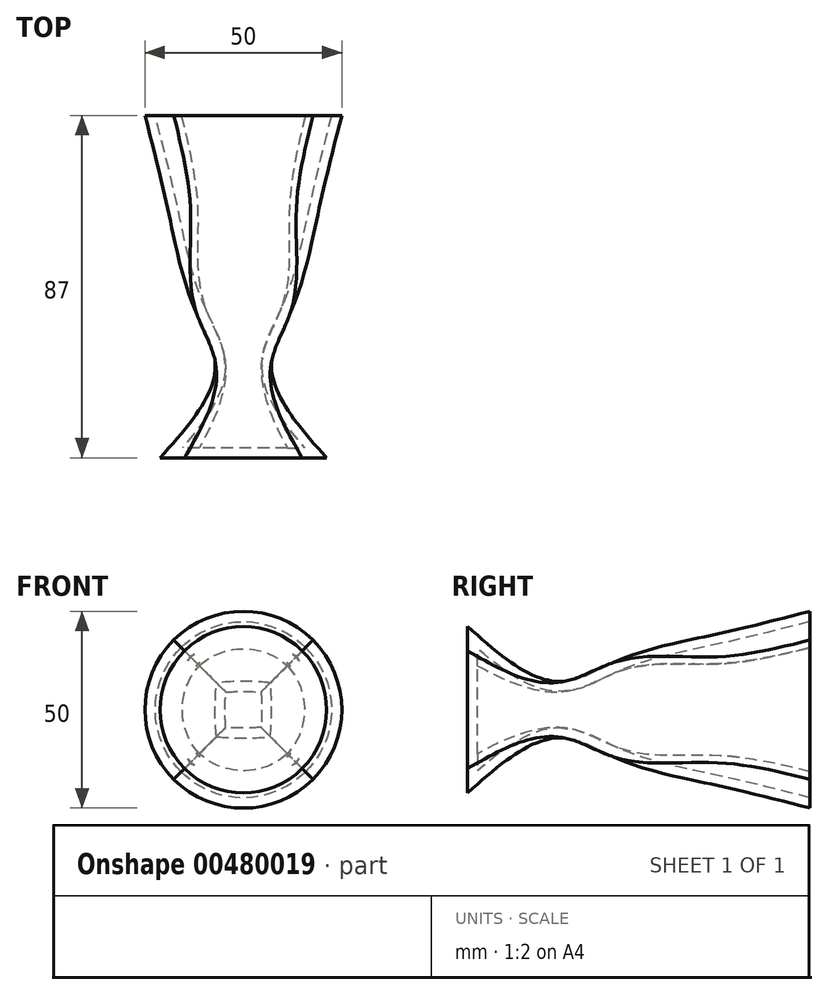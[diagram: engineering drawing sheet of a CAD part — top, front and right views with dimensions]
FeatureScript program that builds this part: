
annotation { "Feature Type Name" : "Feature", "Feature Type Description" : "" }
export const myFeature = defineFeature(function(context is Context, id is Id, definition is map)
    precondition{}
    {
        {
            var Q0;
            Q0=qCreatedBy(makeId("Front.planeOp"),FACE);
            var sketch = newSketch(context, id + "F0", { "sketchPlane" : qUnion([Q0])});
            skCircle(sketch, "E0", {"center": v(0, 0) * mm, "radius": 25 * mm});
            skSolve(sketch);
        }
        {
            var Q0;
            Q0=qCreatedBy(makeId("Front.planeOp"),FACE);
            cPlane(context, id + "F1", {"entities" : qUnion([Q0]), "cplaneType" : CPlaneType.OFFSET, "offset" : 25 * mm, "width" : 152.4 * mm, "height" : 152.4 * mm});
        }
        {
            var Q0;
            Q0=qCreatedBy(id+"F1.planeOp",FACE);
            var sketch = newSketch(context, id + "F2", { "sketchPlane" : qUnion([Q0])});
            skCircle(sketch, "E1", {"center": v(0, 0) * mm, "radius": 18.94 * mm});
            skSolve(sketch);
        }
        {
            var Q0;
            Q0=qCreatedBy(id+"F1.planeOp",FACE);
            cPlane(context, id + "F3", {"entities" : qUnion([Q0]), "cplaneType" : CPlaneType.OFFSET, "offset" : 25 * mm, "width" : 152.4 * mm, "height" : 152.4 * mm});
        }
        {
            var Q0;
            Q0=qCreatedBy(id+"F3.planeOp",FACE);
            var sketch = newSketch(context, id + "F4", { "sketchPlane" : qUnion([Q0])});
            skLineSegment(sketch, "E2.bottom", {"start": v(-11.96, 11.96) * mm, "end": v(11.96, 11.96) * mm});
            skLineSegment(sketch, "E2.top", {"start": v(-11.96, -11.96) * mm, "end": v(11.96, -11.96) * mm});
            skLineSegment(sketch, "E2.left", {"start": v(-11.96, 11.96) * mm, "end": v(-11.96, -11.96) * mm});
            skLineSegment(sketch, "E2.right", {"start": v(11.96, 11.96) * mm, "end": v(11.96, -11.96) * mm});
            skPoint(sketch, "E2.middle", {"position": v(0, 0) * mm});
            skSolve(sketch);
        }
        {
            var Q0;
            Q0=qCreatedBy(id+"F3.planeOp",FACE);
            cPlane(context, id + "F5", {"entities" : qUnion([Q0]), "cplaneType" : CPlaneType.OFFSET, "offset" : 12 * mm, "width" : 152.4 * mm, "height" : 152.4 * mm});
        }
        {
            var Q0;
            Q0=qCreatedBy(id+"F5.planeOp",FACE);
            var sketch = newSketch(context, id + "F6", { "sketchPlane" : qUnion([Q0])});
            skLineSegment(sketch, "E3.bottom", {"start": v(-7.25, 7.25) * mm, "end": v(7.25, 7.25) * mm});
            skLineSegment(sketch, "E3.top", {"start": v(-7.25, -7.25) * mm, "end": v(7.25, -7.25) * mm});
            skLineSegment(sketch, "E3.left", {"start": v(-7.25, 7.25) * mm, "end": v(-7.25, -7.25) * mm});
            skLineSegment(sketch, "E3.right", {"start": v(7.25, 7.25) * mm, "end": v(7.25, -7.25) * mm});
            skPoint(sketch, "E3.middle", {"position": v(0, 0) * mm});
            skSolve(sketch);
        }
        {
            var Q0;
            Q0=qCreatedBy(id+"F5.planeOp",FACE);
            cPlane(context, id + "F7", {"entities" : qUnion([Q0]), "cplaneType" : CPlaneType.OFFSET, "offset" : 25 * mm, "width" : 152.4 * mm, "height" : 152.4 * mm});
        }
        {
            var Q0;
            Q0=qCreatedBy(id+"F7.planeOp",FACE);
            var sketch = newSketch(context, id + "F8", { "sketchPlane" : qUnion([Q0])});
            skCircle(sketch, "E4", {"center": v(0, 0) * mm, "radius": 21.14 * mm});
            skSolve(sketch);
        }
        {
            var Q0;
            Q0=makeQuery(id+"F8.imprint","IMPRINT",FACE,{"disambiguationData":[TD([[makeQuery(id+"F8.imprint","IMPRINT",EDGE,{"derivedFrom":sQuery(id+"F8.wireOp",EDGE,"E4")}),1.0]])]});
            var Q1;
            Q1=makeQuery(id+"F6.imprint","IMPRINT",FACE,{"disambiguationData":[TD([[makeQuery(id+"F6.imprint","IMPRINT",EDGE,{"derivedFrom":sQuery(id+"F6.wireOp",EDGE,"E3.bottom")}),-1.0]])]});
            var Q2;
            Q2=makeQuery(id+"F4.imprint","IMPRINT",FACE,{"disambiguationData":[TD([[makeQuery(id+"F4.imprint","IMPRINT",EDGE,{"derivedFrom":sQuery(id+"F4.wireOp",EDGE,"E2.bottom")}),-1.0]])]});
            var Q3;
            Q3=makeQuery(id+"F2.imprint","IMPRINT",FACE,{"disambiguationData":[TD([[makeQuery(id+"F2.imprint","IMPRINT",EDGE,{"derivedFrom":sQuery(id+"F2.wireOp",EDGE,"E1")}),1.0]])]});
            var Q4;
            Q4=makeQuery(id+"F0.imprint","IMPRINT",FACE,{"disambiguationData":[TD([[makeQuery(id+"F0.imprint","IMPRINT",EDGE,{"derivedFrom":sQuery(id+"F0.wireOp",EDGE,"E0")}),1.0]])]});
            loft(context, id + "F9", {"sheetProfilesArray" : [{ "sheetProfileEntities" : qUnion([Q0]) }, { "sheetProfileEntities" : qUnion([Q1]) }, { "sheetProfileEntities" : qUnion([Q2]) }, { "sheetProfileEntities" : qUnion([Q3]) }, { "sheetProfileEntities" : qUnion([Q4]) }]});
        }
        {
            var Q0;
            Q0=makeQuery(id+"F9.opLoft","CAP_FACE",FACE,{"disambiguationData":[OSD([makeQuery(id+"F0.imprint","IMPRINT",FACE,{"disambiguationData":[TD([[makeQuery(id+"F0.imprint","IMPRINT",EDGE,{"derivedFrom":sQuery(id+"F0.wireOp",EDGE,"E0")}),1.0]])]})])],"isStart":true});
            shell(context, id + "F10", {"entities" : qUnion([Q0]), "thickness" : 2.54 * mm});
        }
    });
